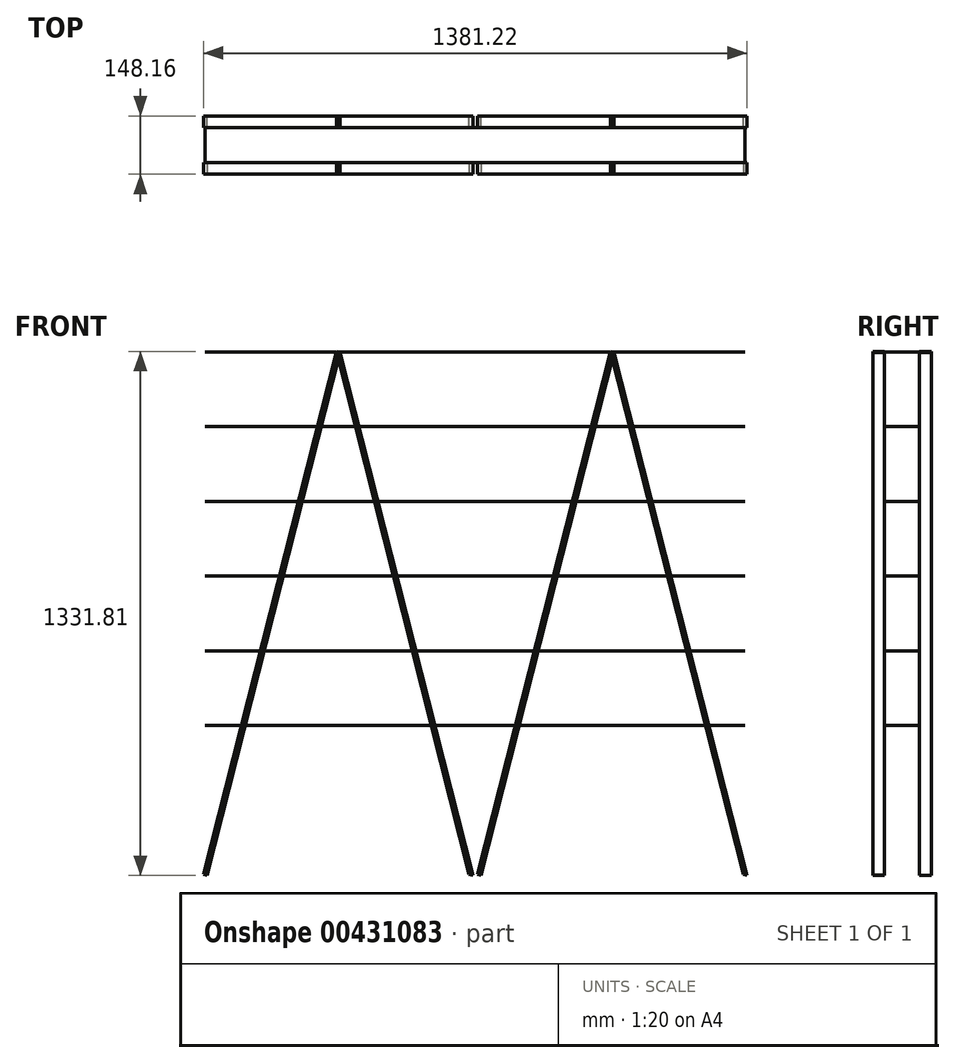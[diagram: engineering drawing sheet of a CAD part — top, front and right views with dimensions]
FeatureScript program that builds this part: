
annotation { "Feature Type Name" : "Feature", "Feature Type Description" : "" }
export const myFeature = defineFeature(function(context is Context, id is Id, definition is map)
    precondition{}
    {
        {
            var Q0;
            Q0=qCreatedBy(makeId("Front.planeOp"),FACE);
            var sketch = newSketch(context, id + "F0", { "sketchPlane" : qUnion([Q0])});
            skLineSegment(sketch, "E0", {"start": v(-53, 736.07) * mm, "end": v(-390.73, -593.3) * mm});
            skLineSegment(sketch, "E1", {"start": v(-53, 736.07) * mm, "end": v(284.75, -593.3) * mm});
            skLineSegment(sketch, "E2", {"start": v(284.75, -593.3) * mm, "end": v(305.39, -593.3) * mm});
            skLineSegment(sketch, "E3", {"start": v(305.39, -593.3) * mm, "end": v(643.13, 736.07) * mm});
            skLineSegment(sketch, "E4", {"start": v(643.13, 736.07) * mm, "end": v(980.87, -593.3) * mm});
            skLineSegment(sketch, "E5", {"start": v(-390.73, -593.3) * mm, "end": v(980.87, -593.3) * mm, "construction": true});
            skLineSegment(sketch, "E6", {"start": v(-390.73, -593.3) * mm, "end": v(-390.73, -645.75) * mm, "construction": true});
            skLineSegment(sketch, "E7", {"start": v(284.75, -593.3) * mm, "end": v(284.75, -645.75) * mm, "construction": true});
            skLineSegment(sketch, "E8", {"start": v(305.39, -593.3) * mm, "end": v(305.39, -645.75) * mm, "construction": true});
            skLineSegment(sketch, "E9", {"start": v(980.87, -593.3) * mm, "end": v(980.87, -645.75) * mm, "construction": true});
            skLineSegment(sketch, "E10", {"start": v(-390.73, -645.75) * mm, "end": v(284.75, -645.75) * mm, "construction": true});
            skLineSegment(sketch, "E11", {"start": v(305.39, -645.75) * mm, "end": v(980.87, -645.75) * mm, "construction": true});
            skLineSegment(sketch, "E12", {"start": v(980.87, 736.07) * mm, "end": v(-390.73, 736.07) * mm});
            skLineSegment(sketch, "E13", {"start": v(980.87, 546.16) * mm, "end": v(-390.73, 546.16) * mm});
            skLineSegment(sketch, "E14", {"start": v(980.87, 356.25) * mm, "end": v(-390.73, 356.25) * mm});
            skLineSegment(sketch, "E15", {"start": v(980.87, 166.34) * mm, "end": v(-390.73, 166.34) * mm});
            skLineSegment(sketch, "E16", {"start": v(980.87, -23.57) * mm, "end": v(-390.73, -23.57) * mm});
            skLineSegment(sketch, "E17", {"start": v(980.87, -213.48) * mm, "end": v(-390.73, -213.48) * mm});
            skLineSegment(sketch, "E18", {"start": v(643.13, 736.07) * mm, "end": v(643.13, 546.16) * mm, "construction": true});
            skLineSegment(sketch, "E19", {"start": v(643.13, 546.16) * mm, "end": v(643.13, 356.25) * mm, "construction": true});
            skLineSegment(sketch, "E20", {"start": v(643.13, 356.25) * mm, "end": v(643.13, 166.34) * mm, "construction": true});
            skLineSegment(sketch, "E21", {"start": v(643.13, 166.34) * mm, "end": v(643.13, -23.57) * mm, "construction": true});
            skLineSegment(sketch, "E22", {"start": v(643.13, -23.57) * mm, "end": v(643.13, -213.48) * mm, "construction": true});
            skLineSegment(sketch, "E23", {"start": v(980.87, -403.4) * mm, "end": v(-390.73, -403.4) * mm, "construction": true});
            skLineSegment(sketch, "E24", {"start": v(643.13, -213.48) * mm, "end": v(643.13, -403.4) * mm});
            skLineSegment(sketch, "E25", {"start": v(643.13, -403.4) * mm, "end": v(643.13, -593.3) * mm});
            skSolve(sketch);
        }
        {
            var Q0;
            Q0=sQuery(id+"F0.wireOp",EDGE,"E12");
            var Q1;
            Q1=sQuery(id+"F0.wireOp",EDGE,"E13");
            var Q2;
            Q2=sQuery(id+"F0.wireOp",EDGE,"E14");
            var Q3;
            Q3=sQuery(id+"F0.wireOp",EDGE,"E15");
            var Q4;
            Q4=sQuery(id+"F0.wireOp",EDGE,"E16");
            var Q5;
            Q5=sQuery(id+"F0.wireOp",EDGE,"E17");
            extrude(context, id + "F1", {"bodyType" : ToolBodyType.SURFACE, "surfaceEntities" : qUnion([Q0, Q1, Q2, Q3, Q4, Q5]), "depth" : 88.9 * mm});
        }
        {
            var Q0;
            Q0=makeQuery(id+"F1.opExtrude","SWEPT_FACE",FACE,{"disambiguationData":[OSD([sQuery(id+"F0.wireOp",EDGE,"E17")])]});
            var Q1;
            Q1=makeQuery(id+"F1.opExtrude","SWEPT_FACE",FACE,{"disambiguationData":[OSD([sQuery(id+"F0.wireOp",EDGE,"E16")])]});
            var Q2;
            Q2=makeQuery(id+"F1.opExtrude","SWEPT_FACE",FACE,{"disambiguationData":[OSD([sQuery(id+"F0.wireOp",EDGE,"E15")])]});
            var Q3;
            Q3=makeQuery(id+"F1.opExtrude","SWEPT_FACE",FACE,{"disambiguationData":[OSD([sQuery(id+"F0.wireOp",EDGE,"E14")])]});
            var Q4;
            Q4=makeQuery(id+"F1.opExtrude","SWEPT_FACE",FACE,{"disambiguationData":[OSD([sQuery(id+"F0.wireOp",EDGE,"E13")])]});
            var Q5;
            Q5=makeQuery(id+"F1.opExtrude","SWEPT_FACE",FACE,{"disambiguationData":[OSD([sQuery(id+"F0.wireOp",EDGE,"E12")])]});
            extrude(context, id + "F2", {"entities" : qUnion([Q0, Q1, Q2, Q3, Q4, Q5]), "depth" : 23 / 1625.6 * mm, "hasSecondDirection" : true, "secondDirectionOppositeDirection" : true, "secondDirectionDepth" : 23 / 1625.6 * mm});
        }
        {
            var Q0;
            Q0=sQuery(id+"F0.wireOp",EDGE,"E0");
            var Q1;
            Q1=sQuery(id+"F0.wireOp",EDGE,"E1");
            var Q2;
            Q2=sQuery(id+"F0.wireOp",EDGE,"E3");
            var Q3;
            Q3=sQuery(id+"F0.wireOp",EDGE,"E4");
            extrude(context, id + "F3", {"bodyType" : ToolBodyType.SURFACE, "surfaceEntities" : qUnion([Q0, Q1, Q2, Q3]), "depth" : -88.9 * mm / 3});
        }
        {
            var Q0;
            Q0=makeQuery(id+"F3.opExtrude","SWEPT_FACE",FACE,{"disambiguationData":[OSD([sQuery(id+"F0.wireOp",EDGE,"E0")])]});
            var Q1;
            Q1=makeQuery(id+"F3.opExtrude","SWEPT_FACE",FACE,{"disambiguationData":[OSD([sQuery(id+"F0.wireOp",EDGE,"E1")])]});
            var Q2;
            Q2=makeQuery(id+"F3.opExtrude","SWEPT_FACE",FACE,{"disambiguationData":[OSD([sQuery(id+"F0.wireOp",EDGE,"E3")])]});
            var Q3;
            Q3=makeQuery(id+"F3.opExtrude","SWEPT_FACE",FACE,{"disambiguationData":[OSD([sQuery(id+"F0.wireOp",EDGE,"E4")])]});
            extrude(context, id + "F4", {"entities" : qUnion([Q0, Q1, Q2, Q3]), "depth" : 9.92 * mm / 2, "hasSecondDirection" : true, "secondDirectionOppositeDirection" : true, "secondDirectionDepth" : 9.92 * mm / 2});
        }
        {
            var Q0;
            {var subQ0=sQuery(id+"F0.wireOp",EDGE,"E15");Q0=makeQuery(id+"F2.opExtrude","SWEPT_FACE",FACE,{"disambiguationData":[OSD([subQ0]),TDD([makeQuery(id+"F1.opExtrude","CAP_EDGE",EDGE,{"disambiguationData":[OSD([subQ0])],"isStart":false})])]});}
            var Q1;
            {var subQ0=sQuery(id+"F0.wireOp",EDGE,"E15");Q1=makeQuery(id+"F2.opExtrude","SWEPT_FACE",FACE,{"disambiguationData":[OSD([subQ0]),TDD([makeQuery(id+"F1.opExtrude","CAP_EDGE",EDGE,{"disambiguationData":[OSD([subQ0])],"isStart":true})])]});}
            cPlane(context, id + "F5", {"entities" : qUnion([Q0, Q1]), "cplaneType" : CPlaneType.MID_PLANE, "offset" : 25.4 * mm, "width" : 152.4 * mm, "height" : 152.4 * mm});
        }
        {
            var Q0;
            Q0=makeQuery(id+"F4.opExtrude","SWEPT_BODY",BODY,{"disambiguationData":[OSD([sQuery(id+"F0.wireOp",EDGE,"E4")])]});
            var Q1;
            Q1=makeQuery(id+"F4.opExtrude","SWEPT_BODY",BODY,{"disambiguationData":[OSD([sQuery(id+"F0.wireOp",EDGE,"E3")])]});
            var Q2;
            Q2=makeQuery(id+"F4.opExtrude","SWEPT_BODY",BODY,{"disambiguationData":[OSD([sQuery(id+"F0.wireOp",EDGE,"E1")])]});
            var Q3;
            Q3=makeQuery(id+"F4.opExtrude","SWEPT_BODY",BODY,{"disambiguationData":[OSD([sQuery(id+"F0.wireOp",EDGE,"E0")])]});
            var Q4;
            Q4=qCreatedBy(id+"F5.planeOp",FACE);
            mirror(context, id + "F6", {"entities" : qUnion([Q0, Q1, Q2, Q3]), "mirrorPlane" : qUnion([Q4])});
        }
    });
